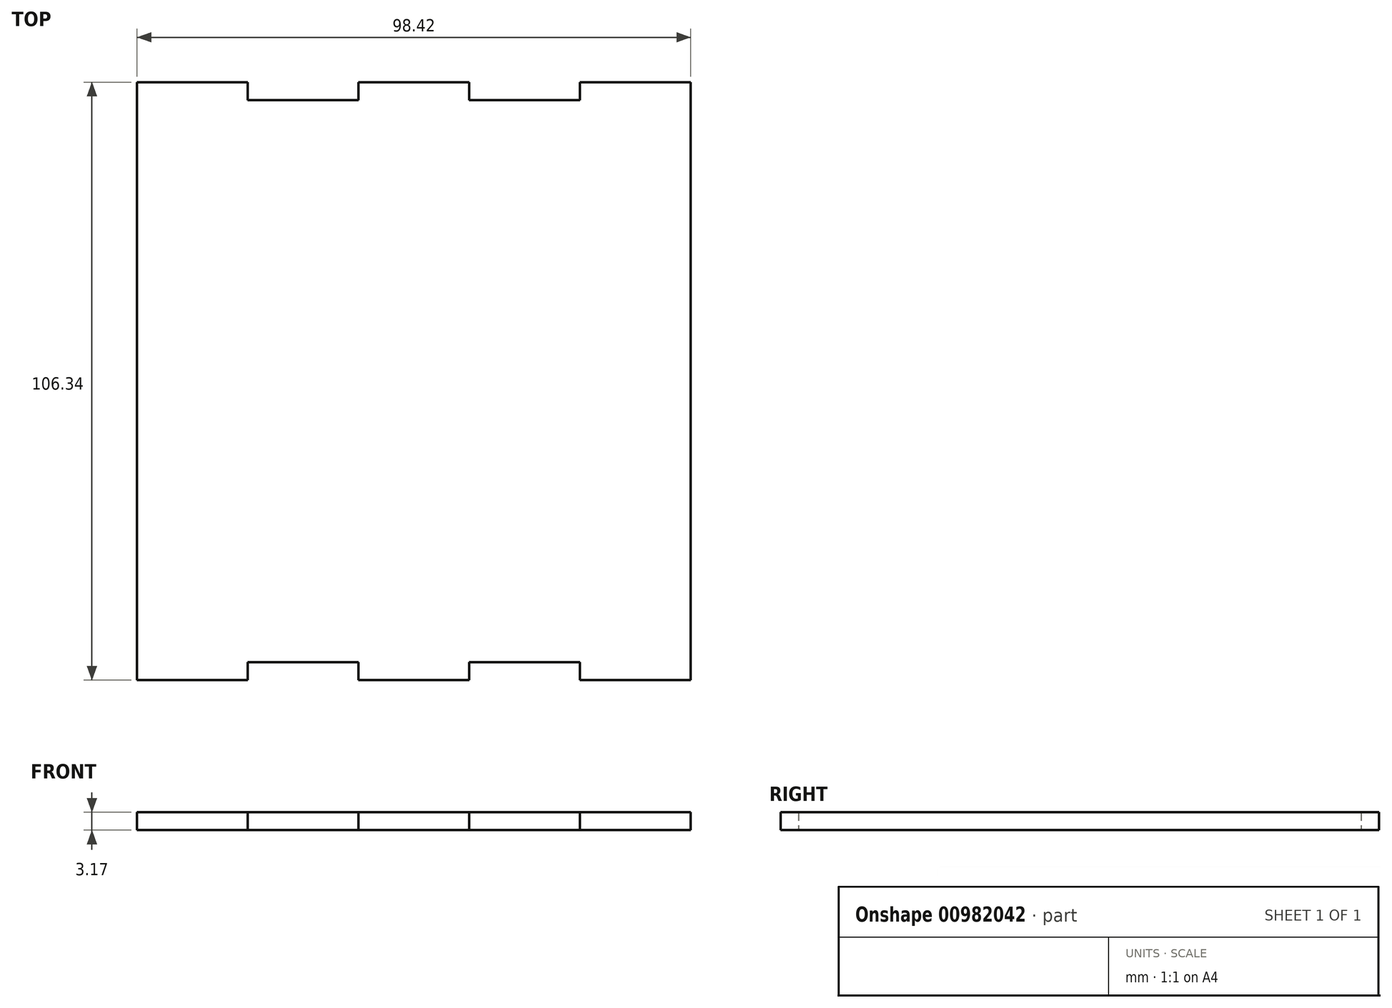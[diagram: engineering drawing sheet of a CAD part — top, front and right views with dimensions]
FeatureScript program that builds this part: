
annotation { "Feature Type Name" : "Feature", "Feature Type Description" : "" }
export const myFeature = defineFeature(function(context is Context, id is Id, definition is map)
    precondition{}
    {
        {
            var Q0;
            Q0=qCreatedBy(makeId("Top.planeOp"),FACE);
            var sketch = newSketch(context, id + "F0", { "sketchPlane" : qUnion([Q0])});
            skLineSegment(sketch, "E0.bottom", {"start": v(49.21, -65) * mm, "end": v(-49.21, -65) * mm, "construction": true});
            skLineSegment(sketch, "E0.top", {"start": v(49.21, 35) * mm, "end": v(-49.21, 35) * mm, "construction": true});
            skPoint(sketch, "E0.middle", {"position": v(0, 0) * mm});
            skLineSegment(sketch, "E1.top", {"start": v(-49.21, 38.17) * mm, "end": v(-29.53, 38.17) * mm});
            skLineSegment(sketch, "E1.left", {"start": v(-49.21, 35) * mm, "end": v(-49.21, 38.17) * mm});
            skLineSegment(sketch, "E1.right", {"start": v(-29.53, 35) * mm, "end": v(-29.53, 38.17) * mm});
            skLineSegment(sketch, "E2.top", {"start": v(49.21, 38.18) * mm, "end": v(29.53, 38.18) * mm});
            skLineSegment(sketch, "E2.left", {"start": v(49.21, 35) * mm, "end": v(49.21, 38.18) * mm});
            skLineSegment(sketch, "E2.right", {"start": v(29.53, 35) * mm, "end": v(29.53, 38.18) * mm});
            skLineSegment(sketch, "E3.top", {"start": v(-9.84, 38.18) * mm, "end": v(9.84, 38.18) * mm});
            skLineSegment(sketch, "E3.left", {"start": v(-9.84, 35) * mm, "end": v(-9.84, 38.18) * mm});
            skLineSegment(sketch, "E3.right", {"start": v(9.84, 35) * mm, "end": v(9.84, 38.18) * mm});
            skLineSegment(sketch, "E4", {"start": v(-29.53, 35) * mm, "end": v(-9.84, 35) * mm});
            skLineSegment(sketch, "E5", {"start": v(9.84, 35) * mm, "end": v(29.53, 35) * mm});
            skLineSegment(sketch, "E6.MirrorCS", {"start": v(-49.21, -65) * mm, "end": v(-49.21, -68.17) * mm});
            skLineSegment(sketch, "E7.MirrorCS", {"start": v(29.53, -65) * mm, "end": v(29.53, -68.18) * mm});
            skLineSegment(sketch, "E8.MirrorCS", {"start": v(-9.84, -65) * mm, "end": v(-9.84, -68.18) * mm});
            skLineSegment(sketch, "E9.MirrorCS", {"start": v(-29.53, -65) * mm, "end": v(-29.53, -68.17) * mm});
            skLineSegment(sketch, "E10.MirrorCS", {"start": v(9.84, -65) * mm, "end": v(9.84, -68.18) * mm});
            skLineSegment(sketch, "E11.MirrorCS", {"start": v(49.21, -65) * mm, "end": v(49.21, -68.18) * mm});
            skLineSegment(sketch, "E12.MirrorCS", {"start": v(9.84, -65) * mm, "end": v(29.53, -65) * mm});
            skLineSegment(sketch, "E13.MirrorCS", {"start": v(-29.53, -65) * mm, "end": v(-9.84, -65) * mm});
            skLineSegment(sketch, "E14.MirrorCS", {"start": v(49.21, -68.18) * mm, "end": v(29.53, -68.17) * mm});
            skLineSegment(sketch, "E15.MirrorCS", {"start": v(-49.21, -68.17) * mm, "end": v(-29.53, -68.17) * mm});
            skLineSegment(sketch, "E16.MirrorCS", {"start": v(-9.84, -68.18) * mm, "end": v(9.84, -68.18) * mm});
            skLineSegment(sketch, "E17", {"start": v(-49.21, 35) * mm, "end": v(-49.21, -65) * mm});
            skLineSegment(sketch, "E18", {"start": v(49.21, 35) * mm, "end": v(49.21, -65) * mm});
            skSolve(sketch);
        }
        {
            var Q0;
            Q0 = qSketchRegion(id + "F0", true);
            extrude(context, id + "F1", {"entities" : qUnion([Q0]), "depth" : 3.17 * mm, "offsetDistance" : 25 * mm});
        }
    });
